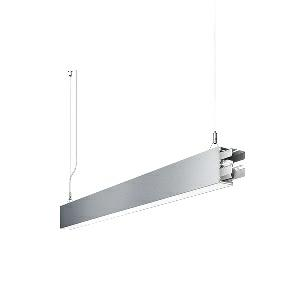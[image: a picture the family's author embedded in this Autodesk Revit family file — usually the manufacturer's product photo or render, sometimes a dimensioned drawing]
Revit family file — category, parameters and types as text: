
# Revit family: idoo_line_-_ilp_3000_830_d_sta_00805726_6a82
name_source: partatom
category: Lighting Fixtures
units: mm (PartAtom-declared; Revit-internal decimal feet)

## family parameters
Cut with Voids When Loaded = No
Host = Face
Light Source = No
Part Type = Normal
Room Calculation Point = No
Round Connector Dimension = Use Diameter
Shared = No

## types (1)
- IDOO.line - ILP 3000/830/D STA (1 x LED, 3000 lm, 3000K)
    Apparent Load = 23 VA
    Approval mark = CE
    CIE Flux Codes = 66 91 98 40 100
    Color Rendering = 80-89
    Color Temperature = 3000K
    Control Gear = Electronic ballast
    Default Elevation = 1800 mm
    Description = ILP 3000/830/D|Suspended luminaire|light source: LED|connected load: 220-240 V, 50/60 Hz|Power consumption: approx. 23 W|standby: approx. 0,20|luminous flux: 3000 lm|luminous efficacy: 130 lm/W|light distribution: Direct/indirect|direct ratio: approx. 40 %|colour temperature: Warm white, ca. 3000 K|color rendering index (CRI): >= 80|chromaticity tolerance:  3 SDCM|System of protection: IP 40|technology: Continuously dimmable|luminaire body|material: Sectional aluminium|colour: Silver|lamp cover: Acrylic (PMMA), Clear|mains lead: 2.00 m With free stranded wires|Fastening: Steel cable 0.3 - 0.7 m|glare control: Prism aperture|luminance(L65): <= 2700 cd/m|unified glare rating(4H 8H): <=  16|special features: DALI Load 1x, TouchDIM - dimming via standard switch, Through-wired, up to 18 m on one mains connection, Flicker-free, Suitable as emergency lighting, Start luminaire with mains connection, Mechanical and electrical connection of the individual modules without tools|
    Frequency = 50 Hz
    Height = 110 mm
    Lamp = 1 x LED
    Lamp Light Flux = 3000 lm
    Lamp count = 1
    Length = 1128 mm
    Luminous efficacy = 130 lm/W
    Manufacturer = Waldmann
    ModVariant = No
    Model = 00805726
    Mounting Place = Ceiling
    Mounting Type = Pendant
    Number of Poles = 1
    OnlyDefault = Yes
    Power Factor = 1
    Product Name = IDOO.line - ILP 3000/830/D STA
    Product group = Suspended luminaire
    ProductGroupID = 9
    Protection Class = Protection class I
    Protection Degree = IP 40
    RLX_Detail_Level = 1
    RLX_Emergency_Light_Flux = 0 lm
    RLX_Emergency_Type = 0
    RLX_Emergency_Type_DB = No
    RlxData = <blob elided: 22277 chars, md5=70d7299f>
    Socket = socket
    Standby Power = 0 W
    System Light Flux = 3000 lm
    System Power = 23 W
    Type Comments = Product without accessories
    Type Image = 113304000-00692576.jpg
    URL = http://relux.com
    VarID = ---
    Voltage = 230 V
    Voltage Range = 220-240 V
    Weight = 0.00 kg
    Width = 60 mm  [stored 0.19685 ft]

note: [stored X ft] marks values corroborated as IEEE doubles in the binary element streams (Revit-internal decimal feet)

## geometry (parser evidence)
native form markers: Blend x4, Sweep x12
no freeform markers — native parametric forms only
